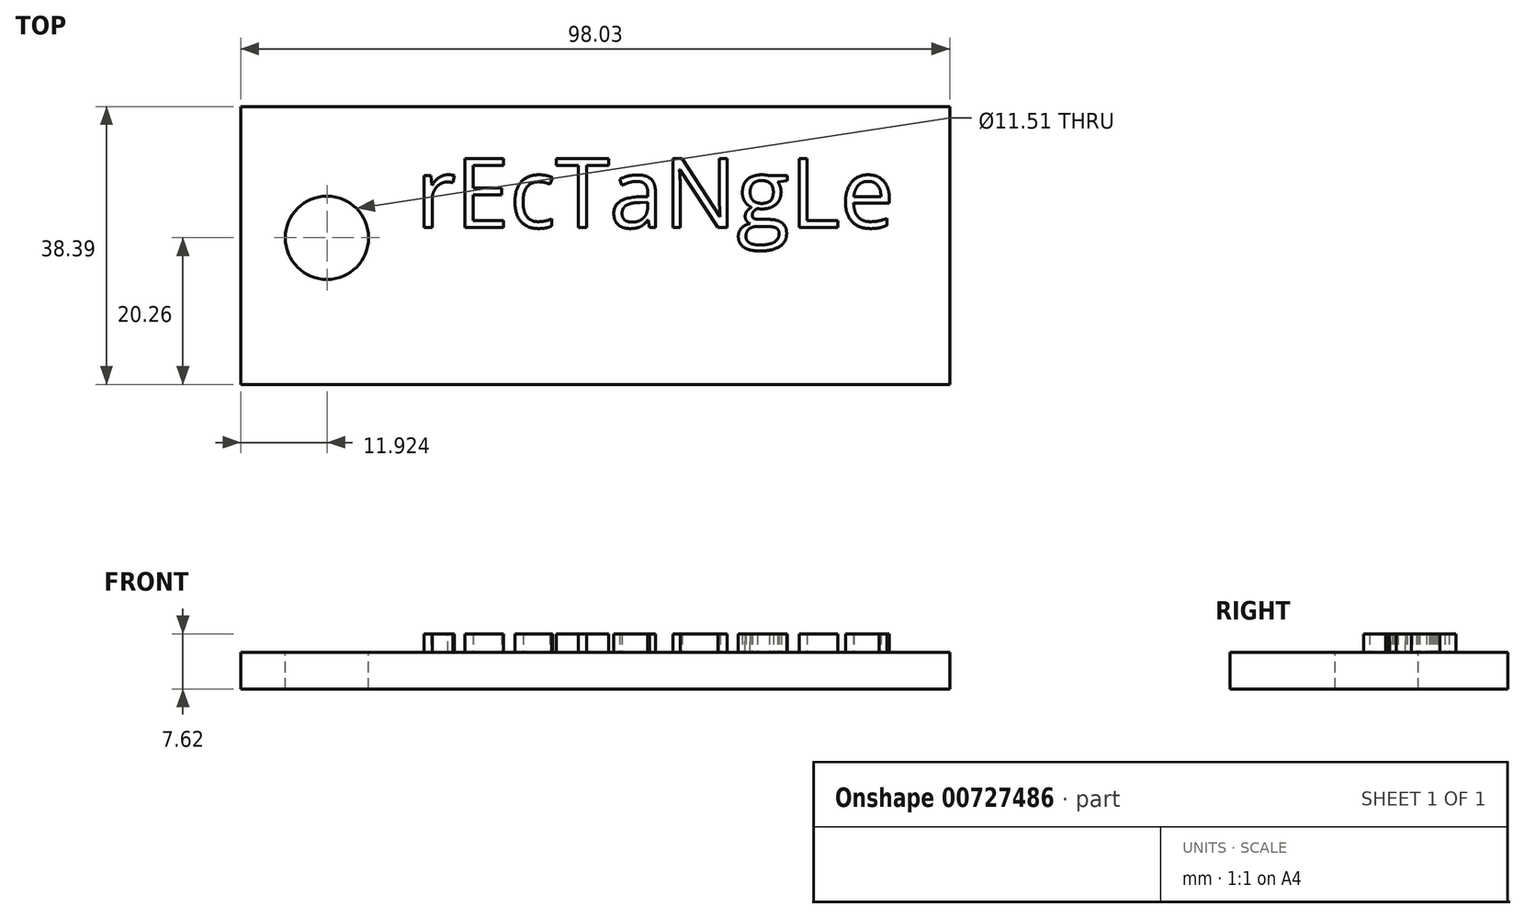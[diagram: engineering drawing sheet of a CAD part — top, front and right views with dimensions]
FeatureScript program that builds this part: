
annotation { "Feature Type Name" : "Feature", "Feature Type Description" : "" }
export const myFeature = defineFeature(function(context is Context, id is Id, definition is map)
    precondition{}
    {
        {
            var Q0;
            Q0=qCreatedBy(makeId("Top.planeOp"),FACE);
            var sketch = newSketch(context, id + "F0", { "sketchPlane" : qUnion([Q0])});
            skLineSegment(sketch, "E0.bottom", {"start": v(-50.41, 18.13) * mm, "end": v(47.62, 18.13) * mm});
            skLineSegment(sketch, "E0.top", {"start": v(-50.41, -20.26) * mm, "end": v(47.62, -20.26) * mm});
            skLineSegment(sketch, "E0.left", {"start": v(-50.41, 18.13) * mm, "end": v(-50.41, -20.26) * mm});
            skLineSegment(sketch, "E0.right", {"start": v(47.62, 18.13) * mm, "end": v(47.62, -20.26) * mm});
            skSolve(sketch);
        }
        {
            var Q0;
            Q0 = qSketchRegion(id + "F0", true);
            extrude(context, id + "F1", {"entities" : qUnion([Q0]), "depth" : 5.08 * mm, "offsetDistance" : 25.4 * mm});
        }
        {
            var Q0;
            Q0=makeQuery(id+"F1.opExtrude","CAP_FACE",FACE,{"disambiguationData":[OSD([sQuery(id+"F0.wireOp",EDGE,"E0.bottom"),sQuery(id+"F0.wireOp",EDGE,"E0.top"),sQuery(id+"F0.wireOp",EDGE,"E0.left"),sQuery(id+"F0.wireOp",EDGE,"E0.right")])],"isStart":false});
            var sketch = newSketch(context, id + "F2", { "sketchPlane" : qUnion([Q0])});
            skCircle(sketch, "E1", {"center": v(-38.49, 0) * mm, "radius": 5.75 * mm});
            skSolve(sketch);
        }
        {
            var Q0;
            Q0 = qSketchRegion(id + "F2", true);
            extrude(context, id + "F3", {"entities" : qUnion([Q0]), "operationType" : NewBodyOperationType.REMOVE, "oppositeDirection" : true, "depth" : 25.4 * mm, "offsetDistance" : 25.4 * mm});
        }
        {
            var Q0;
            Q0=makeQuery(id+"F1.opExtrude","CAP_FACE",FACE,{"disambiguationData":[OSD([sQuery(id+"F0.wireOp",EDGE,"E0.bottom"),sQuery(id+"F0.wireOp",EDGE,"E0.top"),sQuery(id+"F0.wireOp",EDGE,"E0.left"),sQuery(id+"F0.wireOp",EDGE,"E0.right")])],"isStart":false});
            var sketch = newSketch(context, id + "F4", { "sketchPlane" : qUnion([Q0])});
            skText(sketch, "E2", { "text": "rEcTaNgLe", "fontName": "OpenSans-Regular.ttf"});
            const initialGuessF4  = {"E2": [-0.02619, 0.0014, 1, 0, 0.00966]};
            skSetInitialGuess(sketch, initialGuessF4);
            skSolve(sketch);
        }
        {
            var Q0;
            Q0 = qSketchRegion(id + "F4", true);
            extrude(context, id + "F5", {"entities" : qUnion([Q0]), "operationType" : NewBodyOperationType.ADD, "depth" : 2.54 * mm, "offsetDistance" : 25.4 * mm});
        }
    });
